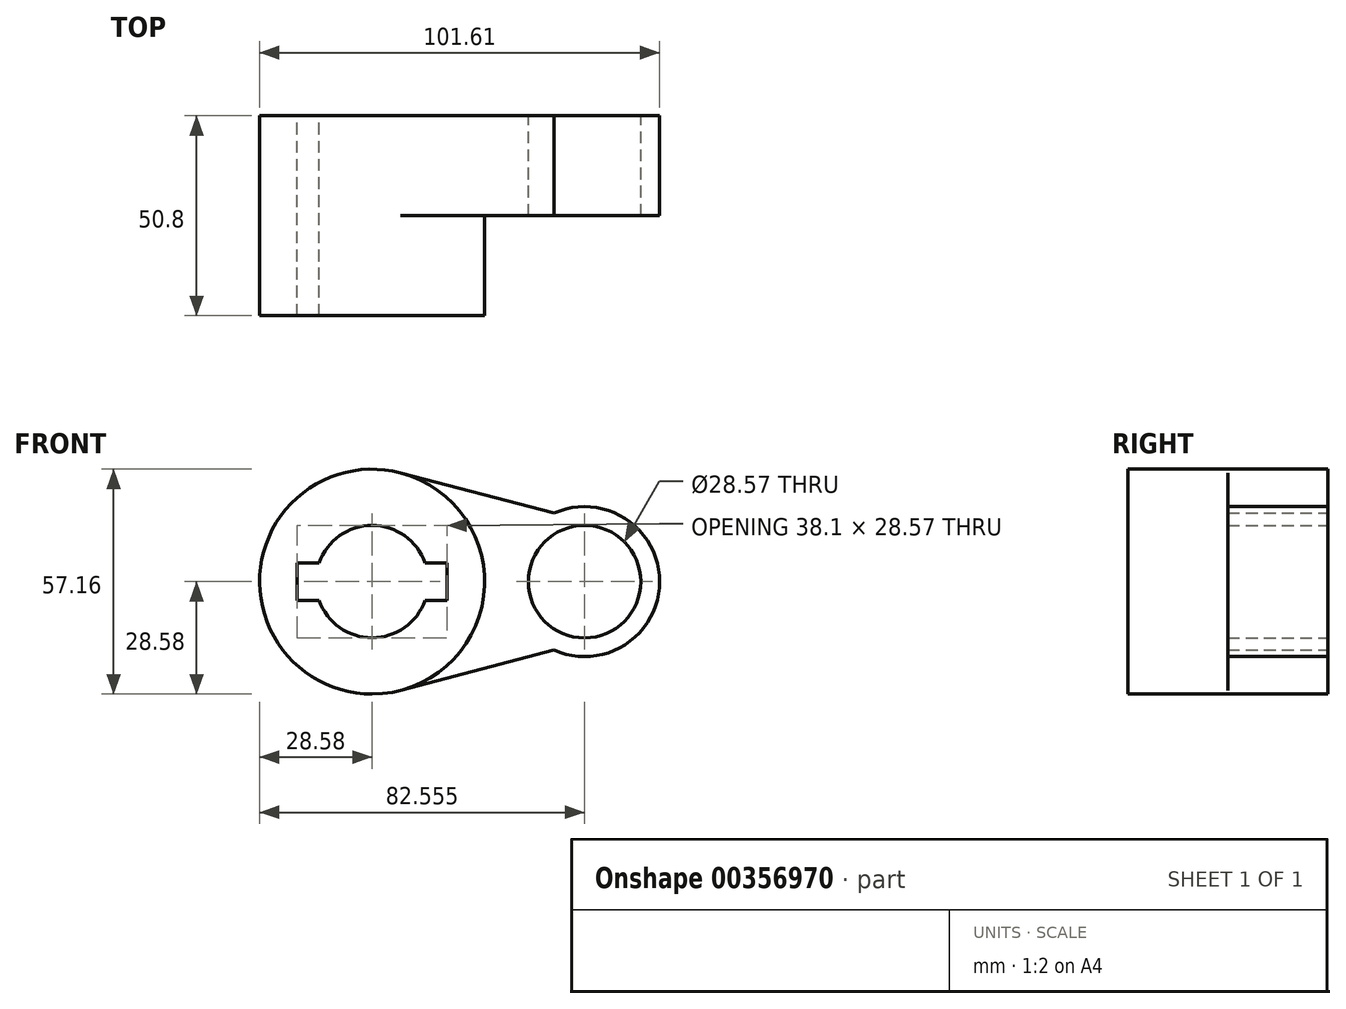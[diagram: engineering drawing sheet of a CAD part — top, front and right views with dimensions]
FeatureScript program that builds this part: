
annotation { "Feature Type Name" : "Feature", "Feature Type Description" : "" }
export const myFeature = defineFeature(function(context is Context, id is Id, definition is map)
    precondition{}
    {
        {
            var Q0;
            Q0=qCreatedBy(makeId("Front.planeOp"),FACE);
            var sketch = newSketch(context, id + "F0", { "sketchPlane" : qUnion([Q0])});
            skCircle(sketch, "E0", {"center": v(0, 0) * mm, "radius": 28.58 * mm});
            skCircle(sketch, "E1", {"center": v(53.98, 0) * mm, "radius": 19.05 * mm});
            skLineSegment(sketch, "E2", {"start": v(7.28, 27.63) * mm, "end": v(46.18, 17.38) * mm});
            skLineSegment(sketch, "E3", {"start": v(7.28, -27.63) * mm, "end": v(46.18, -17.38) * mm});
            skCircle(sketch, "E4", {"center": v(0, 0) * mm, "radius": 14.29 * mm});
            skCircle(sketch, "E5", {"center": v(53.98, 0) * mm, "radius": 14.29 * mm});
            skLineSegment(sketch, "E6.bottom", {"start": v(-19.05, -4.76) * mm, "end": v(19.05, -4.76) * mm});
            skLineSegment(sketch, "E6.top", {"start": v(-19.05, 4.76) * mm, "end": v(19.05, 4.76) * mm});
            skLineSegment(sketch, "E6.left", {"start": v(-19.05, -4.76) * mm, "end": v(-19.05, 4.76) * mm});
            skLineSegment(sketch, "E6.right", {"start": v(19.05, -4.76) * mm, "end": v(19.05, 4.76) * mm});
            skSolve(sketch);
        }
        {
            var Q0;
            {var subQ7=sQuery(id+"F0.wireOp",EDGE,"E6.left");Q0=makeQuery(id+"F0.imprint","IMPRINT",FACE,{"disambiguationData":[TD([[makeQuery(id+"F0.imprint","IMPRINT",EDGE,{"derivedFrom":subQ7}),1.0]])]});}
            var Q1;
            {var subQ0=sQuery(id+"F0.wireOp",EDGE,"E2");Q1=makeQuery(id+"F0.imprint","IMPRINT",FACE,{"disambiguationData":[TD([[makeQuery(id+"F0.imprint","IMPRINT",EDGE,{"derivedFrom":subQ0}),-1.0]])]});}
            var Q2;
            Q2=makeQuery(id+"F0.imprint","IMPRINT",FACE,{"disambiguationData":[TD([[makeQuery(id+"F0.imprint","IMPRINT",EDGE,{"derivedFrom":sQuery(id+"F0.wireOp",EDGE,"E5")}),-1.0]])]});
            extrude(context, id + "F1", {"entities" : qUnion([Q0, Q1, Q2]), "depth" : 25.4 * mm});
        }
        {
            var Q0;
            {var subQ7=sQuery(id+"F0.wireOp",EDGE,"E6.left");Q0=makeQuery(id+"F0.imprint","IMPRINT",FACE,{"disambiguationData":[TD([[makeQuery(id+"F0.imprint","IMPRINT",EDGE,{"derivedFrom":subQ7}),1.0]])]});}
            extrude(context, id + "F2", {"entities" : qUnion([Q0]), "operationType" : NewBodyOperationType.ADD, "depth" : 50.8 * mm});
        }
    });
